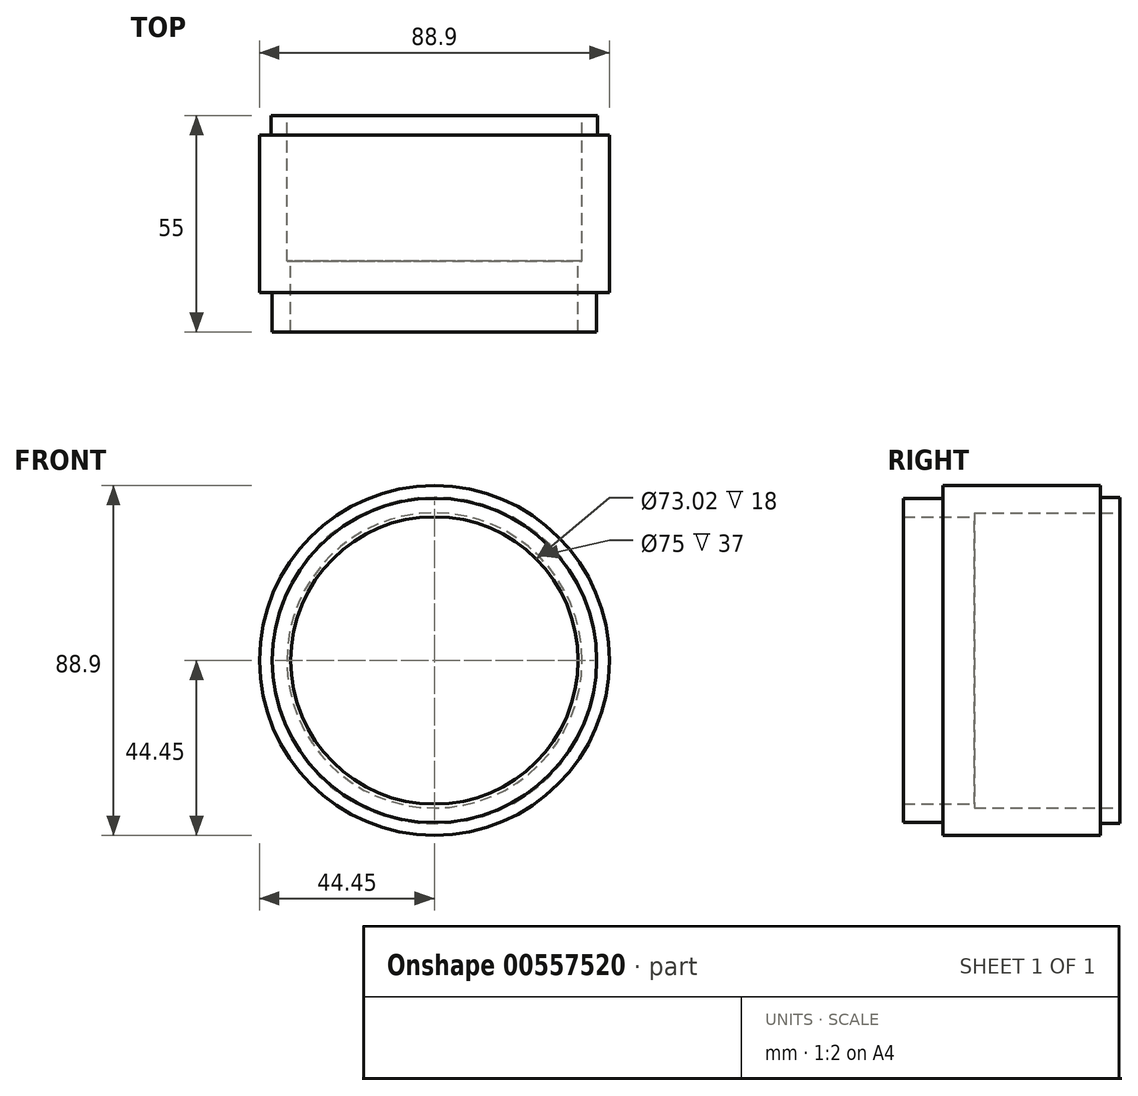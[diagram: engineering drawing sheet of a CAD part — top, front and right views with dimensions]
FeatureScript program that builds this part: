
annotation { "Feature Type Name" : "Feature", "Feature Type Description" : "" }
export const myFeature = defineFeature(function(context is Context, id is Id, definition is map)
    precondition{}
    {
        {
            var Q0;
            Q0=qCreatedBy(makeId("Front.planeOp"),FACE);
            var sketch = newSketch(context, id + "F0", { "sketchPlane" : qUnion([Q0])});
            skCircle(sketch, "E0", {"center": v(0, 0) * mm, "radius": 36.5 * mm});
            skCircle(sketch, "E1", {"center": v(0, 0) * mm, "radius": 44.45 * mm});
            skSolve(sketch);
        }
        {
            var Q0;
            Q0=makeQuery(id+"F0.imprint","IMPRINT",FACE,{"disambiguationData":[TD([[makeQuery(id+"F0.imprint","IMPRINT",EDGE,{"derivedFrom":sQuery(id+"F0.wireOp",EDGE,"E0")}),-1.0]])]});
            extrude(context, id + "F1", {"entities" : qUnion([Q0]), "depth" : 55 * mm, "offsetDistance" : 25 * mm});
        }
        {
            var Q0;
            Q0=makeQuery(id+"F1.opExtrude","CAP_FACE",FACE,{"disambiguationData":[OSD([sQuery(id+"F0.wireOp",EDGE,"E0"),sQuery(id+"F0.wireOp",EDGE,"E1")])],"isStart":false});
            var sketch = newSketch(context, id + "F2", { "sketchPlane" : qUnion([Q0])});
            skCircle(sketch, "E2", {"center": v(0, 0) * mm, "radius": 41.2 * mm});
            skCircle(sketch, "E3", {"center": v(0, 0) * mm, "radius": 44.45 * mm});
            skSolve(sketch);
        }
        {
            var Q0;
            Q0=makeQuery(id+"F2.imprint","IMPRINT",FACE,{"disambiguationData":[TD([[makeQuery(id+"F2.imprint","IMPRINT",EDGE,{"derivedFrom":sQuery(id+"F2.wireOp",EDGE,"E2")}),-1.0]])]});
            extrude(context, id + "F3", {"entities" : qUnion([Q0]), "operationType" : NewBodyOperationType.REMOVE, "oppositeDirection" : true, "depth" : 10 * mm, "offsetDistance" : 25 * mm});
        }
        {
            var Q0;
            Q0=makeQuery(id+"F1.opExtrude","CAP_FACE",FACE,{"disambiguationData":[OSD([sQuery(id+"F0.wireOp",EDGE,"E0"),sQuery(id+"F0.wireOp",EDGE,"E1")])],"isStart":true});
            var sketch = newSketch(context, id + "F4", { "sketchPlane" : qUnion([Q0])});
            skCircle(sketch, "E4.0", {"center": v(0, 0) * mm, "radius": 41.45 * mm});
            skCircle(sketch, "E5", {"center": v(0, 0) * mm, "radius": 37.5 * mm});
            skSolve(sketch);
        }
        {
            var Q0;
            Q0=makeQuery(id+"F4.imprint","IMPRINT",FACE,{"disambiguationData":[TD([[makeQuery(id+"F4.imprint","IMPRINT",EDGE,{"derivedFrom":sQuery(id+"F4.wireOp",EDGE,"E4.0")}),-1.0]])]});
            extrude(context, id + "F5", {"entities" : qUnion([Q0]), "operationType" : NewBodyOperationType.REMOVE, "oppositeDirection" : true, "depth" : 5 * mm, "offsetDistance" : 25 * mm});
        }
        {
            var Q0;
            Q0=makeQuery(id+"F4.imprint","IMPRINT",FACE,{"disambiguationData":[TD([[makeQuery(id+"F4.imprint","IMPRINT",EDGE,{"derivedFrom":sQuery(id+"F4.wireOp",EDGE,"E5")}),1.0]])]});
            extrude(context, id + "F6", {"entities" : qUnion([Q0]), "operationType" : NewBodyOperationType.REMOVE, "oppositeDirection" : true, "depth" : 37 * mm, "offsetDistance" : 25 * mm});
        }
    });
